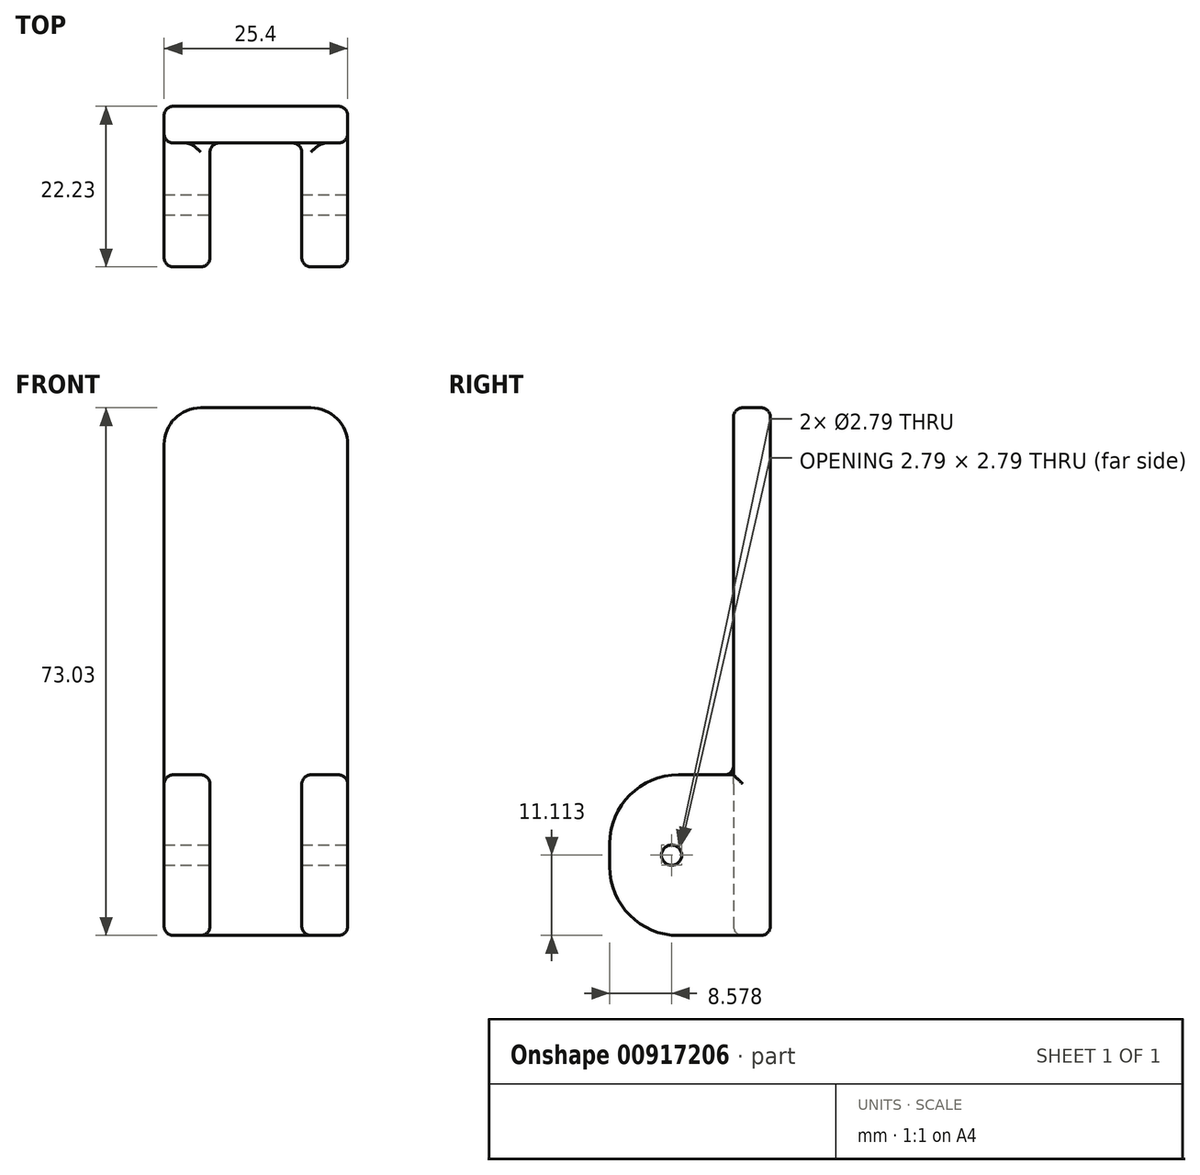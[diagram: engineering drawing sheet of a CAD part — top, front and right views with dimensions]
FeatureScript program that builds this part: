
annotation { "Feature Type Name" : "Feature", "Feature Type Description" : "" }
export const myFeature = defineFeature(function(context is Context, id is Id, definition is map)
    precondition{}
    {
        {
            var Q0;
            Q0=qCreatedBy(makeId("Top.planeOp"),FACE);
            var sketch = newSketch(context, id + "F0", { "sketchPlane" : qUnion([Q0])});
            skLineSegment(sketch, "E0", {"start": v(-12.7, 0) * mm, "end": v(12.7, 0) * mm});
            skLineSegment(sketch, "E1", {"start": v(12.7, 0) * mm, "end": v(12.7, -22.23) * mm});
            skLineSegment(sketch, "E2", {"start": v(12.7, -22.22) * mm, "end": v(6.35, -22.22) * mm});
            skLineSegment(sketch, "E3", {"start": v(6.35, -22.23) * mm, "end": v(6.35, -5.08) * mm});
            skLineSegment(sketch, "E4", {"start": v(6.35, -5.08) * mm, "end": v(-6.35, -5.08) * mm});
            skLineSegment(sketch, "E5", {"start": v(-6.35, -5.08) * mm, "end": v(-6.35, -22.23) * mm});
            skLineSegment(sketch, "E6", {"start": v(-6.35, -22.23) * mm, "end": v(-12.7, -22.23) * mm});
            skLineSegment(sketch, "E7", {"start": v(-12.7, -22.23) * mm, "end": v(-12.7, 0) * mm});
            skSolve(sketch);
        }
        {
            var Q0;
            Q0=makeQuery(id+"F0.imprint","IMPRINT",FACE,{"disambiguationData":[TD([[makeQuery(id+"F0.imprint","IMPRINT",EDGE,{"derivedFrom":sQuery(id+"F0.wireOp",EDGE,"E0")}),-1.0]])]});
            extrude(context, id + "F1", {"entities" : qUnion([Q0]), "depth" : 22.22 * mm, "offsetDistance" : 25.4 * mm});
        }
        {
            var Q0;
            Q0=makeQuery(id+"F1.opExtrude","CAP_FACE",FACE,{"disambiguationData":[OSD([sQuery(id+"F0.wireOp",EDGE,"E0"),sQuery(id+"F0.wireOp",EDGE,"E1"),sQuery(id+"F0.wireOp",EDGE,"E2"),sQuery(id+"F0.wireOp",EDGE,"E3"),sQuery(id+"F0.wireOp",EDGE,"E4"),sQuery(id+"F0.wireOp",EDGE,"E5"),sQuery(id+"F0.wireOp",EDGE,"E6"),sQuery(id+"F0.wireOp",EDGE,"E7")])],"isStart":false});
            var sketch = newSketch(context, id + "F2", { "sketchPlane" : qUnion([Q0])});
            skLineSegment(sketch, "E8.bottom", {"start": v(-12.7, 0) * mm, "end": v(12.7, 0) * mm});
            skLineSegment(sketch, "E8.top", {"start": v(-12.7, -5.08) * mm, "end": v(12.7, -5.08) * mm});
            skLineSegment(sketch, "E8.left", {"start": v(-12.7, 0) * mm, "end": v(-12.7, -5.08) * mm});
            skLineSegment(sketch, "E8.right", {"start": v(12.7, 0) * mm, "end": v(12.7, -5.08) * mm});
            skSolve(sketch);
        }
        {
            var Q0;
            Q0=makeQuery(id+"F2.imprint","IMPRINT",FACE,{"disambiguationData":[TD([[makeQuery(id+"F2.imprint","IMPRINT",EDGE,{"derivedFrom":sQuery(id+"F2.wireOp",EDGE,"E8.bottom")}),-1.0]])]});
            extrude(context, id + "F3", {"entities" : qUnion([Q0]), "operationType" : NewBodyOperationType.ADD, "depth" : 50.8 * mm, "offsetDistance" : 25.4 * mm});
        }
        {
            var Q0;
            Q0=makeQuery(id+"F3.boolean.opBoolean","MERGE",FACE,{"derivedFrom":[makeQuery(id+"F1.opExtrude","SWEPT_FACE",FACE,{"disambiguationData":[OSD([sQuery(id+"F0.wireOp",EDGE,"E1")])]}),makeQuery(id+"F3.opExtrude","SWEPT_FACE",FACE,{"disambiguationData":[OSD([sQuery(id+"F2.wireOp",EDGE,"E8.right")])]})]});
            var sketch = newSketch(context, id + "F4", { "sketchPlane" : qUnion([Q0])});
            skCircle(sketch, "E9", {"center": v(-13.65, 11.11) * mm, "radius": 1.4 * mm});
            skLineSegment(sketch, "E10", {"start": v(-22.23, 11.11) * mm, "end": v(-40.67, 11.11) * mm, "construction": true});
            skLineSegment(sketch, "E11", {"start": v(-13.65, 22.23) * mm, "end": v(-13.65, -2.66) * mm, "construction": true});
            skSolve(sketch);
        }
        {
            var Q0;
            Q0=makeQuery(id+"F4.imprint","IMPRINT",FACE,{"disambiguationData":[TD([[makeQuery(id+"F4.imprint","IMPRINT",EDGE,{"derivedFrom":sQuery(id+"F4.wireOp",EDGE,"E9")}),1.0]])]});
            extrude(context, id + "F5", {"entities" : qUnion([Q0]), "operationType" : NewBodyOperationType.REMOVE, "endBound" : BoundingType.THROUGH_ALL, "oppositeDirection" : true, "depth" : 25.4 * mm, "offsetDistance" : 25.4 * mm});
        }
        {
            var Q0;
            Q0=makeQuery(id+"F1.opExtrude","CAP_EDGE",EDGE,{"disambiguationData":[OSD([sQuery(id+"F0.wireOp",EDGE,"E2")])],"isStart":false});
            var Q1;
            Q1=makeQuery(id+"F1.opExtrude","CAP_EDGE",EDGE,{"disambiguationData":[OSD([sQuery(id+"F0.wireOp",EDGE,"E6")])],"isStart":false});
            var Q2;
            Q2=makeQuery(id+"F1.opExtrude","CAP_EDGE",EDGE,{"disambiguationData":[OSD([sQuery(id+"F0.wireOp",EDGE,"E6")])],"isStart":true});
            var Q3;
            Q3=makeQuery(id+"F1.opExtrude","CAP_EDGE",EDGE,{"disambiguationData":[OSD([sQuery(id+"F0.wireOp",EDGE,"E2")])],"isStart":true});
            fillet(context, id + "F6", {"entities" : qUnion([Q0, Q1, Q2, Q3]), "radius" : 9.52 * mm, "tangentPropagation" : true, "allowEdgeOverflow" : false});
        }
        {
            var Q0;
            Q0=makeQuery(id+"F3.opExtrude","CAP_EDGE",EDGE,{"disambiguationData":[OSD([sQuery(id+"F2.wireOp",EDGE,"E8.right")])],"isStart":false});
            var Q1;
            Q1=makeQuery(id+"F3.opExtrude","CAP_EDGE",EDGE,{"disambiguationData":[OSD([sQuery(id+"F2.wireOp",EDGE,"E8.left")])],"isStart":false});
            var Q2;
            {var subQ2=sQuery(id+"F0.wireOp",EDGE,"E1");var subQ3=sQuery(id+"F2.wireOp",EDGE,"E8.top");Q2=makeQuery(id+"F3.boolean.opBoolean","SPLIT",EDGE,{"disambiguationData":[TD([makeQuery(id+"F1.opExtrude","SWEPT_FACE",FACE,{"disambiguationData":[OSD([subQ2])]})])],"derivedFrom":makeQuery(id+"F3.opExtrude","CAP_EDGE",EDGE,{"disambiguationData":[OSD([subQ3])],"isStart":true})});}
            var Q3;
            {var subQ2=sQuery(id+"F0.wireOp",EDGE,"E5");var subQ3=sQuery(id+"F2.wireOp",EDGE,"E8.top");Q3=makeQuery(id+"F3.boolean.opBoolean","SPLIT",EDGE,{"disambiguationData":[TD([makeQuery(id+"F1.opExtrude","SWEPT_FACE",FACE,{"disambiguationData":[OSD([subQ2])]})])],"derivedFrom":makeQuery(id+"F3.opExtrude","CAP_EDGE",EDGE,{"disambiguationData":[OSD([subQ3])],"isStart":true})});}
            fillet(context, id + "F7", {"entities" : qUnion([Q0, Q1, Q2, Q3]), "radius" : 5.08 * mm, "tangentPropagation" : true, "allowEdgeOverflow" : false});
        }
        {
            var Q0;
            Q0=makeQuery(id+"F6.opFillet","BLEND_EDGE",EDGE,{"blendedFrom":[makeQuery(id+"F1.opExtrude","CAP_EDGE",EDGE,{"disambiguationData":[OSD([sQuery(id+"F0.wireOp",EDGE,"E6")])],"isStart":true}),makeQuery(id+"F3.boolean.opBoolean","MERGE",FACE,{"derivedFrom":[makeQuery(id+"F1.opExtrude","SWEPT_FACE",FACE,{"disambiguationData":[OSD([sQuery(id+"F0.wireOp",EDGE,"E7")])]}),makeQuery(id+"F3.opExtrude","SWEPT_FACE",FACE,{"disambiguationData":[OSD([sQuery(id+"F2.wireOp",EDGE,"E8.left")])]})]})],"blendedInto":[makeQuery(id+"F3.boolean.opBoolean","MERGE",FACE,{"derivedFrom":[makeQuery(id+"F1.opExtrude","SWEPT_FACE",FACE,{"disambiguationData":[OSD([sQuery(id+"F0.wireOp",EDGE,"E7")])]}),makeQuery(id+"F3.opExtrude","SWEPT_FACE",FACE,{"disambiguationData":[OSD([sQuery(id+"F2.wireOp",EDGE,"E8.left")])]})]})]});
            var Q1;
            Q1=makeQuery(id+"F6.opFillet","BLEND_EDGE",EDGE,{"blendedFrom":[makeQuery(id+"F1.opExtrude","CAP_EDGE",EDGE,{"disambiguationData":[OSD([sQuery(id+"F0.wireOp",EDGE,"E6")])],"isStart":false}),makeQuery(id+"F3.boolean.opBoolean","MERGE",FACE,{"derivedFrom":[makeQuery(id+"F1.opExtrude","SWEPT_FACE",FACE,{"disambiguationData":[OSD([sQuery(id+"F0.wireOp",EDGE,"E7")])]}),makeQuery(id+"F3.opExtrude","SWEPT_FACE",FACE,{"disambiguationData":[OSD([sQuery(id+"F2.wireOp",EDGE,"E8.left")])]})]})],"blendedInto":[makeQuery(id+"F3.boolean.opBoolean","MERGE",FACE,{"derivedFrom":[makeQuery(id+"F1.opExtrude","SWEPT_FACE",FACE,{"disambiguationData":[OSD([sQuery(id+"F0.wireOp",EDGE,"E7")])]}),makeQuery(id+"F3.opExtrude","SWEPT_FACE",FACE,{"disambiguationData":[OSD([sQuery(id+"F2.wireOp",EDGE,"E8.left")])]})]})]});
            var Q2;
            Q2=makeQuery(id+"F6.opFillet","BLEND_EDGE",EDGE,{"blendedFrom":[makeQuery(id+"F1.opExtrude","CAP_EDGE",EDGE,{"disambiguationData":[OSD([sQuery(id+"F0.wireOp",EDGE,"E6")])],"isStart":true}),makeQuery(id+"F1.opExtrude","SWEPT_FACE",FACE,{"disambiguationData":[OSD([sQuery(id+"F0.wireOp",EDGE,"E5")])]})],"blendedInto":[makeQuery(id+"F1.opExtrude","SWEPT_FACE",FACE,{"disambiguationData":[OSD([sQuery(id+"F0.wireOp",EDGE,"E5")])]})]});
            var Q3;
            Q3=makeQuery(id+"F7.opFillet","BLEND_EDGE",EDGE,{"blendedFrom":[makeQuery(id+"F3.opExtrude","CAP_EDGE",EDGE,{"disambiguationData":[OSD([sQuery(id+"F2.wireOp",EDGE,"E8.right")])],"isStart":false}),makeQuery(id+"F3.boolean.opBoolean","MERGE",FACE,{"derivedFrom":[makeQuery(id+"F1.opExtrude","SWEPT_FACE",FACE,{"disambiguationData":[OSD([sQuery(id+"F0.wireOp",EDGE,"E4")])]}),makeQuery(id+"F3.opExtrude","SWEPT_FACE",FACE,{"disambiguationData":[OSD([sQuery(id+"F2.wireOp",EDGE,"E8.top")])]})]})],"blendedInto":[makeQuery(id+"F3.boolean.opBoolean","MERGE",FACE,{"derivedFrom":[makeQuery(id+"F1.opExtrude","SWEPT_FACE",FACE,{"disambiguationData":[OSD([sQuery(id+"F0.wireOp",EDGE,"E4")])]}),makeQuery(id+"F3.opExtrude","SWEPT_FACE",FACE,{"disambiguationData":[OSD([sQuery(id+"F2.wireOp",EDGE,"E8.top")])]})]})]});
            var Q4;
            Q4=makeQuery(id+"F3.boolean.opBoolean","MERGE",EDGE,{"derivedFrom":[makeQuery(id+"F1.opExtrude","SWEPT_EDGE",EDGE,{"disambiguationData":[OSD([sQuery(id+"F0.wireOp",EDGE,"E0"),sQuery(id+"F0.wireOp",EDGE,"E1")])]}),makeQuery(id+"F3.opExtrude","SWEPT_EDGE",EDGE,{"disambiguationData":[OSD([sQuery(id+"F2.wireOp",EDGE,"E8.bottom"),sQuery(id+"F2.wireOp",EDGE,"E8.right")])]})]});
            var Q5;
            Q5=makeQuery(id+"F3.opExtrude","SWEPT_EDGE",EDGE,{"disambiguationData":[OSD([sQuery(id+"F0.wireOp",EDGE,"E7"),sQuery(id+"F2.wireOp",EDGE,"E8.top"),sQuery(id+"F2.wireOp",EDGE,"E8.left")])]});
            var Q6;
            Q6=makeQuery(id+"F6.opFillet","BLEND_EDGE",EDGE,{"blendedFrom":[makeQuery(id+"F1.opExtrude","CAP_EDGE",EDGE,{"disambiguationData":[OSD([sQuery(id+"F0.wireOp",EDGE,"E6")])],"isStart":false}),makeQuery(id+"F1.opExtrude","SWEPT_FACE",FACE,{"disambiguationData":[OSD([sQuery(id+"F0.wireOp",EDGE,"E5")])]})],"blendedInto":[makeQuery(id+"F1.opExtrude","SWEPT_FACE",FACE,{"disambiguationData":[OSD([sQuery(id+"F0.wireOp",EDGE,"E5")])]})]});
            var Q7;
            Q7=makeQuery(id+"F3.opExtrude","SWEPT_EDGE",EDGE,{"disambiguationData":[OSD([sQuery(id+"F0.wireOp",EDGE,"E1"),sQuery(id+"F2.wireOp",EDGE,"E8.top"),sQuery(id+"F2.wireOp",EDGE,"E8.right")])]});
            var Q8;
            Q8=makeQuery(id+"F6.opFillet","BLEND_EDGE",EDGE,{"blendedFrom":[makeQuery(id+"F1.opExtrude","CAP_EDGE",EDGE,{"disambiguationData":[OSD([sQuery(id+"F0.wireOp",EDGE,"E2")])],"isStart":false}),makeQuery(id+"F1.opExtrude","SWEPT_FACE",FACE,{"disambiguationData":[OSD([sQuery(id+"F0.wireOp",EDGE,"E3")])]})],"blendedInto":[makeQuery(id+"F1.opExtrude","SWEPT_FACE",FACE,{"disambiguationData":[OSD([sQuery(id+"F0.wireOp",EDGE,"E3")])]})]});
            var Q9;
            Q9=makeQuery(id+"F6.opFillet","BLEND_EDGE",EDGE,{"blendedFrom":[makeQuery(id+"F1.opExtrude","CAP_EDGE",EDGE,{"disambiguationData":[OSD([sQuery(id+"F0.wireOp",EDGE,"E2")])],"isStart":false}),makeQuery(id+"F3.boolean.opBoolean","MERGE",FACE,{"derivedFrom":[makeQuery(id+"F1.opExtrude","SWEPT_FACE",FACE,{"disambiguationData":[OSD([sQuery(id+"F0.wireOp",EDGE,"E1")])]}),makeQuery(id+"F3.opExtrude","SWEPT_FACE",FACE,{"disambiguationData":[OSD([sQuery(id+"F2.wireOp",EDGE,"E8.right")])]})]})],"blendedInto":[makeQuery(id+"F3.boolean.opBoolean","MERGE",FACE,{"derivedFrom":[makeQuery(id+"F1.opExtrude","SWEPT_FACE",FACE,{"disambiguationData":[OSD([sQuery(id+"F0.wireOp",EDGE,"E1")])]}),makeQuery(id+"F3.opExtrude","SWEPT_FACE",FACE,{"disambiguationData":[OSD([sQuery(id+"F2.wireOp",EDGE,"E8.right")])]})]})]});
            var Q10;
            {var subQ0=sQuery(id+"F2.wireOp",EDGE,"E8.top");var subQ1=makeQuery(id+"F3.opExtrude","SWEPT_FACE",FACE,{"disambiguationData":[OSD([subQ0])]});var subQ2=sQuery(id+"F0.wireOp",EDGE,"E4");var subQ3=makeQuery(id+"F1.opExtrude","SWEPT_FACE",FACE,{"disambiguationData":[OSD([subQ2])]});var subQ5=sQuery(id+"F0.wireOp",EDGE,"E5");Q10=makeQuery(id+"F7.opFillet","BLEND_EDGE",EDGE,{"blendedFrom":[makeQuery(id+"F3.boolean.opBoolean","SPLIT",EDGE,{"disambiguationData":[TD([makeQuery(id+"F1.opExtrude","SWEPT_FACE",FACE,{"disambiguationData":[OSD([subQ5])]})])],"derivedFrom":makeQuery(id+"F3.opExtrude","CAP_EDGE",EDGE,{"disambiguationData":[OSD([subQ0])],"isStart":true})}),makeQuery(id+"F3.boolean.opBoolean","MERGE",FACE,{"derivedFrom":[subQ3,subQ1]})],"blendedInto":[makeQuery(id+"F3.boolean.opBoolean","MERGE",FACE,{"derivedFrom":[subQ3,subQ1]})]});}
            var Q11;
            Q11=makeQuery(id+"F6.opFillet","BLEND_EDGE",EDGE,{"blendedFrom":[makeQuery(id+"F1.opExtrude","CAP_EDGE",EDGE,{"disambiguationData":[OSD([sQuery(id+"F0.wireOp",EDGE,"E2")])],"isStart":true}),makeQuery(id+"F3.boolean.opBoolean","MERGE",FACE,{"derivedFrom":[makeQuery(id+"F1.opExtrude","SWEPT_FACE",FACE,{"disambiguationData":[OSD([sQuery(id+"F0.wireOp",EDGE,"E1")])]}),makeQuery(id+"F3.opExtrude","SWEPT_FACE",FACE,{"disambiguationData":[OSD([sQuery(id+"F2.wireOp",EDGE,"E8.right")])]})]})],"blendedInto":[makeQuery(id+"F3.boolean.opBoolean","MERGE",FACE,{"derivedFrom":[makeQuery(id+"F1.opExtrude","SWEPT_FACE",FACE,{"disambiguationData":[OSD([sQuery(id+"F0.wireOp",EDGE,"E1")])]}),makeQuery(id+"F3.opExtrude","SWEPT_FACE",FACE,{"disambiguationData":[OSD([sQuery(id+"F2.wireOp",EDGE,"E8.right")])]})]})]});
            var Q12;
            {var subQ0=sQuery(id+"F0.wireOp",EDGE,"E4");var subQ2=sQuery(id+"F0.wireOp",EDGE,"E3");var subQ4=sQuery(id+"F0.wireOp",EDGE,"E2");var subQ5=sQuery(id+"F0.wireOp",EDGE,"E1");var subQ6=makeQuery(id+"F1.opExtrude","SWEPT_FACE",FACE,{"disambiguationData":[OSD([subQ5])]});var subQ7=sQuery(id+"F2.wireOp",EDGE,"E8.top");var subQ10=makeQuery(id+"F1.opExtrude","CAP_FACE",FACE,{"disambiguationData":[OSD([sQuery(id+"F0.wireOp",EDGE,"E0"),subQ5,subQ4,subQ2,subQ0,sQuery(id+"F0.wireOp",EDGE,"E5"),sQuery(id+"F0.wireOp",EDGE,"E6"),sQuery(id+"F0.wireOp",EDGE,"E7")])],"isStart":false});Q12=makeQuery(id+"F7.opFillet","BLEND_EDGE",EDGE,{"blendedFrom":[makeQuery(id+"F3.boolean.opBoolean","SPLIT",EDGE,{"disambiguationData":[TD([subQ6])],"derivedFrom":makeQuery(id+"F3.opExtrude","CAP_EDGE",EDGE,{"disambiguationData":[OSD([subQ7])],"isStart":true})}),makeQuery(id+"F3.boolean.opBoolean","SPLIT",FACE,{"disambiguationData":[TD([subQ6])],"derivedFrom":subQ10})],"blendedInto":[makeQuery(id+"F3.boolean.opBoolean","SPLIT",FACE,{"disambiguationData":[TD([subQ6])],"derivedFrom":subQ10})]});}
            var Q13;
            Q13=makeQuery(id+"F3.opExtrude","CAP_EDGE",EDGE,{"disambiguationData":[OSD([sQuery(id+"F2.wireOp",EDGE,"E8.top")])],"isStart":false});
            var Q14;
            {var subQ0=sQuery(id+"F0.wireOp",EDGE,"E5");var subQ1=makeQuery(id+"F1.opExtrude","SWEPT_FACE",FACE,{"disambiguationData":[OSD([subQ0])]});var subQ4=sQuery(id+"F2.wireOp",EDGE,"E8.top");Q14=makeQuery(id+"F7.opFillet","BLEND_EDGE",EDGE,{"blendedFrom":[makeQuery(id+"F3.boolean.opBoolean","SPLIT",EDGE,{"disambiguationData":[TD([subQ1])],"derivedFrom":makeQuery(id+"F3.opExtrude","CAP_EDGE",EDGE,{"disambiguationData":[OSD([subQ4])],"isStart":true})}),subQ1],"blendedInto":[subQ1]});}
            var Q15;
            Q15=makeQuery(id+"F1.opExtrude","CAP_EDGE",EDGE,{"disambiguationData":[OSD([sQuery(id+"F0.wireOp",EDGE,"E7")])],"isStart":true});
            var Q16;
            Q16=makeQuery(id+"F1.opExtrude","CAP_EDGE",EDGE,{"disambiguationData":[OSD([sQuery(id+"F0.wireOp",EDGE,"E5")])],"isStart":true});
            var Q17;
            Q17=makeQuery(id+"F1.opExtrude","CAP_EDGE",EDGE,{"disambiguationData":[OSD([sQuery(id+"F0.wireOp",EDGE,"E1")])],"isStart":true});
            var Q18;
            Q18=makeQuery(id+"F1.opExtrude","SWEPT_EDGE",EDGE,{"disambiguationData":[OSD([sQuery(id+"F0.wireOp",EDGE,"E3"),sQuery(id+"F0.wireOp",EDGE,"E4")])]});
            var Q19;
            {var subQ0=sQuery(id+"F0.wireOp",EDGE,"E6");Q19=makeQuery(id+"F6.opFillet","BLEND_EDGE",EDGE,{"blendedFrom":[makeQuery(id+"F1.opExtrude","CAP_EDGE",EDGE,{"disambiguationData":[OSD([subQ0])],"isStart":true}),makeQuery(id+"F1.opExtrude","SWEPT_FACE",FACE,{"disambiguationData":[OSD([subQ0])]})],"blendedInto":[makeQuery(id+"F1.opExtrude","SWEPT_FACE",FACE,{"disambiguationData":[OSD([subQ0])]})]});}
            var Q20;
            Q20=makeQuery(id+"F1.opExtrude","SWEPT_EDGE",EDGE,{"disambiguationData":[OSD([sQuery(id+"F0.wireOp",EDGE,"E4"),sQuery(id+"F0.wireOp",EDGE,"E5")])]});
            var Q21;
            Q21=makeQuery(id+"F1.opExtrude","CAP_EDGE",EDGE,{"disambiguationData":[OSD([sQuery(id+"F0.wireOp",EDGE,"E3")])],"isStart":false});
            var Q22;
            Q22=makeQuery(id+"F7.opFillet","BLEND_EDGE",EDGE,{"blendedFrom":[makeQuery(id+"F3.opExtrude","CAP_EDGE",EDGE,{"disambiguationData":[OSD([sQuery(id+"F2.wireOp",EDGE,"E8.left")])],"isStart":false}),makeQuery(id+"F3.boolean.opBoolean","MERGE",FACE,{"derivedFrom":[makeQuery(id+"F1.opExtrude","SWEPT_FACE",FACE,{"disambiguationData":[OSD([sQuery(id+"F0.wireOp",EDGE,"E4")])]}),makeQuery(id+"F3.opExtrude","SWEPT_FACE",FACE,{"disambiguationData":[OSD([sQuery(id+"F2.wireOp",EDGE,"E8.top")])]})]})],"blendedInto":[makeQuery(id+"F3.boolean.opBoolean","MERGE",FACE,{"derivedFrom":[makeQuery(id+"F1.opExtrude","SWEPT_FACE",FACE,{"disambiguationData":[OSD([sQuery(id+"F0.wireOp",EDGE,"E4")])]}),makeQuery(id+"F3.opExtrude","SWEPT_FACE",FACE,{"disambiguationData":[OSD([sQuery(id+"F2.wireOp",EDGE,"E8.top")])]})]})]});
            var Q23;
            {var subQ0=sQuery(id+"F0.wireOp",EDGE,"E6");Q23=makeQuery(id+"F6.opFillet","BLEND_EDGE",EDGE,{"blendedFrom":[makeQuery(id+"F1.opExtrude","CAP_EDGE",EDGE,{"disambiguationData":[OSD([subQ0])],"isStart":true}),makeQuery(id+"F1.opExtrude","CAP_FACE",FACE,{"disambiguationData":[OSD([sQuery(id+"F0.wireOp",EDGE,"E0"),sQuery(id+"F0.wireOp",EDGE,"E1"),sQuery(id+"F0.wireOp",EDGE,"E2"),sQuery(id+"F0.wireOp",EDGE,"E3"),sQuery(id+"F0.wireOp",EDGE,"E4"),sQuery(id+"F0.wireOp",EDGE,"E5"),subQ0,sQuery(id+"F0.wireOp",EDGE,"E7")])],"isStart":true})],"blendedInto":[makeQuery(id+"F1.opExtrude","CAP_FACE",FACE,{"disambiguationData":[OSD([sQuery(id+"F0.wireOp",EDGE,"E0"),sQuery(id+"F0.wireOp",EDGE,"E1"),sQuery(id+"F0.wireOp",EDGE,"E2"),sQuery(id+"F0.wireOp",EDGE,"E3"),sQuery(id+"F0.wireOp",EDGE,"E4"),sQuery(id+"F0.wireOp",EDGE,"E5"),subQ0,sQuery(id+"F0.wireOp",EDGE,"E7")])],"isStart":true})]});}
            var Q24;
            Q24=makeQuery(id+"F1.opExtrude","CAP_EDGE",EDGE,{"disambiguationData":[OSD([sQuery(id+"F0.wireOp",EDGE,"E5")])],"isStart":false});
            var Q25;
            {var subQ0=sQuery(id+"F0.wireOp",EDGE,"E2");Q25=makeQuery(id+"F6.opFillet","BLEND_EDGE",EDGE,{"blendedFrom":[makeQuery(id+"F1.opExtrude","CAP_EDGE",EDGE,{"disambiguationData":[OSD([subQ0])],"isStart":true}),makeQuery(id+"F1.opExtrude","CAP_FACE",FACE,{"disambiguationData":[OSD([sQuery(id+"F0.wireOp",EDGE,"E0"),sQuery(id+"F0.wireOp",EDGE,"E1"),subQ0,sQuery(id+"F0.wireOp",EDGE,"E3"),sQuery(id+"F0.wireOp",EDGE,"E4"),sQuery(id+"F0.wireOp",EDGE,"E5"),sQuery(id+"F0.wireOp",EDGE,"E6"),sQuery(id+"F0.wireOp",EDGE,"E7")])],"isStart":true})],"blendedInto":[makeQuery(id+"F1.opExtrude","CAP_FACE",FACE,{"disambiguationData":[OSD([sQuery(id+"F0.wireOp",EDGE,"E0"),sQuery(id+"F0.wireOp",EDGE,"E1"),subQ0,sQuery(id+"F0.wireOp",EDGE,"E3"),sQuery(id+"F0.wireOp",EDGE,"E4"),sQuery(id+"F0.wireOp",EDGE,"E5"),sQuery(id+"F0.wireOp",EDGE,"E6"),sQuery(id+"F0.wireOp",EDGE,"E7")])],"isStart":true})]});}
            var Q26;
            Q26=makeQuery(id+"F1.opExtrude","CAP_EDGE",EDGE,{"disambiguationData":[OSD([sQuery(id+"F0.wireOp",EDGE,"E1")])],"isStart":false});
            var Q27;
            {var subQ0=sQuery(id+"F0.wireOp",EDGE,"E3");var subQ1=makeQuery(id+"F1.opExtrude","SWEPT_FACE",FACE,{"disambiguationData":[OSD([subQ0])]});var subQ3=sQuery(id+"F0.wireOp",EDGE,"E1");var subQ4=sQuery(id+"F2.wireOp",EDGE,"E8.top");Q27=makeQuery(id+"F7.opFillet","BLEND_EDGE",EDGE,{"blendedFrom":[makeQuery(id+"F3.boolean.opBoolean","SPLIT",EDGE,{"disambiguationData":[TD([makeQuery(id+"F1.opExtrude","SWEPT_FACE",FACE,{"disambiguationData":[OSD([subQ3])]})])],"derivedFrom":makeQuery(id+"F3.opExtrude","CAP_EDGE",EDGE,{"disambiguationData":[OSD([subQ4])],"isStart":true})}),subQ1],"blendedInto":[subQ1]});}
            var Q28;
            Q28=makeQuery(id+"F1.opExtrude","SWEPT_EDGE",EDGE,{"disambiguationData":[OSD([sQuery(id+"F0.wireOp",EDGE,"E6"),sQuery(id+"F0.wireOp",EDGE,"E7")])]});
            var Q29;
            Q29=makeQuery(id+"F3.boolean.opBoolean","MERGE",EDGE,{"derivedFrom":[makeQuery(id+"F1.opExtrude","SWEPT_EDGE",EDGE,{"disambiguationData":[OSD([sQuery(id+"F0.wireOp",EDGE,"E0"),sQuery(id+"F0.wireOp",EDGE,"E7")])]}),makeQuery(id+"F3.opExtrude","SWEPT_EDGE",EDGE,{"disambiguationData":[OSD([sQuery(id+"F2.wireOp",EDGE,"E8.bottom"),sQuery(id+"F2.wireOp",EDGE,"E8.left")])]})]});
            var Q30;
            {var subQ0=makeQuery(id+"F3.opExtrude","SWEPT_FACE",FACE,{"disambiguationData":[OSD([sQuery(id+"F2.wireOp",EDGE,"E8.right")])]});var subQ1=sQuery(id+"F0.wireOp",EDGE,"E1");var subQ2=makeQuery(id+"F1.opExtrude","SWEPT_FACE",FACE,{"disambiguationData":[OSD([subQ1])]});var subQ5=sQuery(id+"F2.wireOp",EDGE,"E8.top");Q30=makeQuery(id+"F7.opFillet","BLEND_EDGE",EDGE,{"blendedFrom":[makeQuery(id+"F3.boolean.opBoolean","SPLIT",EDGE,{"disambiguationData":[TD([subQ2])],"derivedFrom":makeQuery(id+"F3.opExtrude","CAP_EDGE",EDGE,{"disambiguationData":[OSD([subQ5])],"isStart":true})}),makeQuery(id+"F3.boolean.opBoolean","MERGE",FACE,{"derivedFrom":[subQ2,subQ0]})],"blendedInto":[makeQuery(id+"F3.boolean.opBoolean","MERGE",FACE,{"derivedFrom":[subQ2,subQ0]})]});}
            var Q31;
            Q31=makeQuery(id+"F7.opFillet","BLEND_EDGE",EDGE,{"blendedFrom":[makeQuery(id+"F3.opExtrude","CAP_EDGE",EDGE,{"disambiguationData":[OSD([sQuery(id+"F2.wireOp",EDGE,"E8.right")])],"isStart":false}),makeQuery(id+"F3.boolean.opBoolean","MERGE",FACE,{"derivedFrom":[makeQuery(id+"F1.opExtrude","SWEPT_FACE",FACE,{"disambiguationData":[OSD([sQuery(id+"F0.wireOp",EDGE,"E0")])]}),makeQuery(id+"F3.opExtrude","SWEPT_FACE",FACE,{"disambiguationData":[OSD([sQuery(id+"F2.wireOp",EDGE,"E8.bottom")])]})]})],"blendedInto":[makeQuery(id+"F3.boolean.opBoolean","MERGE",FACE,{"derivedFrom":[makeQuery(id+"F1.opExtrude","SWEPT_FACE",FACE,{"disambiguationData":[OSD([sQuery(id+"F0.wireOp",EDGE,"E0")])]}),makeQuery(id+"F3.opExtrude","SWEPT_FACE",FACE,{"disambiguationData":[OSD([sQuery(id+"F2.wireOp",EDGE,"E8.bottom")])]})]})]});
            var Q32;
            {var subQ0=sQuery(id+"F0.wireOp",EDGE,"E4");var subQ1=sQuery(id+"F0.wireOp",EDGE,"E3");var subQ2=sQuery(id+"F0.wireOp",EDGE,"E2");var subQ3=sQuery(id+"F0.wireOp",EDGE,"E1");Q32=makeQuery(id+"F6.opFillet","BLEND_EDGE",EDGE,{"blendedFrom":[makeQuery(id+"F1.opExtrude","CAP_EDGE",EDGE,{"disambiguationData":[OSD([subQ2])],"isStart":false}),makeQuery(id+"F3.boolean.opBoolean","SPLIT",FACE,{"disambiguationData":[TD([makeQuery(id+"F1.opExtrude","SWEPT_FACE",FACE,{"disambiguationData":[OSD([subQ3])]})])],"derivedFrom":makeQuery(id+"F1.opExtrude","CAP_FACE",FACE,{"disambiguationData":[OSD([sQuery(id+"F0.wireOp",EDGE,"E0"),subQ3,subQ2,subQ1,subQ0,sQuery(id+"F0.wireOp",EDGE,"E5"),sQuery(id+"F0.wireOp",EDGE,"E6"),sQuery(id+"F0.wireOp",EDGE,"E7")])],"isStart":false})})],"blendedInto":[makeQuery(id+"F3.boolean.opBoolean","SPLIT",FACE,{"disambiguationData":[TD([makeQuery(id+"F1.opExtrude","SWEPT_FACE",FACE,{"disambiguationData":[OSD([subQ3])]})])],"derivedFrom":makeQuery(id+"F1.opExtrude","CAP_FACE",FACE,{"disambiguationData":[OSD([sQuery(id+"F0.wireOp",EDGE,"E0"),subQ3,subQ2,subQ1,subQ0,sQuery(id+"F0.wireOp",EDGE,"E5"),sQuery(id+"F0.wireOp",EDGE,"E6"),sQuery(id+"F0.wireOp",EDGE,"E7")])],"isStart":false})})]});}
            var Q33;
            {var subQ0=sQuery(id+"F0.wireOp",EDGE,"E6");Q33=makeQuery(id+"F6.opFillet","BLEND_EDGE",EDGE,{"blendedFrom":[makeQuery(id+"F1.opExtrude","CAP_EDGE",EDGE,{"disambiguationData":[OSD([subQ0])],"isStart":false}),makeQuery(id+"F1.opExtrude","SWEPT_FACE",FACE,{"disambiguationData":[OSD([subQ0])]})],"blendedInto":[makeQuery(id+"F1.opExtrude","SWEPT_FACE",FACE,{"disambiguationData":[OSD([subQ0])]})]});}
            var Q34;
            Q34=makeQuery(id+"F6.opFillet","BLEND_EDGE",EDGE,{"blendedFrom":[makeQuery(id+"F1.opExtrude","CAP_EDGE",EDGE,{"disambiguationData":[OSD([sQuery(id+"F0.wireOp",EDGE,"E2")])],"isStart":true}),makeQuery(id+"F1.opExtrude","SWEPT_FACE",FACE,{"disambiguationData":[OSD([sQuery(id+"F0.wireOp",EDGE,"E3")])]})],"blendedInto":[makeQuery(id+"F1.opExtrude","SWEPT_FACE",FACE,{"disambiguationData":[OSD([sQuery(id+"F0.wireOp",EDGE,"E3")])]})]});
            var Q35;
            Q35=makeQuery(id+"F1.opExtrude","CAP_EDGE",EDGE,{"disambiguationData":[OSD([sQuery(id+"F0.wireOp",EDGE,"E0")])],"isStart":true});
            var Q36;
            {var subQ0=sQuery(id+"F0.wireOp",EDGE,"E7");var subQ1=sQuery(id+"F0.wireOp",EDGE,"E6");var subQ2=sQuery(id+"F0.wireOp",EDGE,"E5");var subQ3=sQuery(id+"F0.wireOp",EDGE,"E4");Q36=makeQuery(id+"F6.opFillet","BLEND_EDGE",EDGE,{"blendedFrom":[makeQuery(id+"F1.opExtrude","CAP_EDGE",EDGE,{"disambiguationData":[OSD([subQ1])],"isStart":false}),makeQuery(id+"F3.boolean.opBoolean","SPLIT",FACE,{"disambiguationData":[TD([makeQuery(id+"F1.opExtrude","SWEPT_FACE",FACE,{"disambiguationData":[OSD([subQ2])]})])],"derivedFrom":makeQuery(id+"F1.opExtrude","CAP_FACE",FACE,{"disambiguationData":[OSD([sQuery(id+"F0.wireOp",EDGE,"E0"),sQuery(id+"F0.wireOp",EDGE,"E1"),sQuery(id+"F0.wireOp",EDGE,"E2"),sQuery(id+"F0.wireOp",EDGE,"E3"),subQ3,subQ2,subQ1,subQ0])],"isStart":false})})],"blendedInto":[makeQuery(id+"F3.boolean.opBoolean","SPLIT",FACE,{"disambiguationData":[TD([makeQuery(id+"F1.opExtrude","SWEPT_FACE",FACE,{"disambiguationData":[OSD([subQ2])]})])],"derivedFrom":makeQuery(id+"F1.opExtrude","CAP_FACE",FACE,{"disambiguationData":[OSD([sQuery(id+"F0.wireOp",EDGE,"E0"),sQuery(id+"F0.wireOp",EDGE,"E1"),sQuery(id+"F0.wireOp",EDGE,"E2"),sQuery(id+"F0.wireOp",EDGE,"E3"),subQ3,subQ2,subQ1,subQ0])],"isStart":false})})]});}
            var Q37;
            {var subQ0=sQuery(id+"F2.wireOp",EDGE,"E8.right");Q37=makeQuery(id+"F7.opFillet","BLEND_EDGE",EDGE,{"blendedFrom":[makeQuery(id+"F3.opExtrude","CAP_EDGE",EDGE,{"disambiguationData":[OSD([subQ0])],"isStart":false}),makeQuery(id+"F3.boolean.opBoolean","MERGE",FACE,{"derivedFrom":[makeQuery(id+"F1.opExtrude","SWEPT_FACE",FACE,{"disambiguationData":[OSD([sQuery(id+"F0.wireOp",EDGE,"E1")])]}),makeQuery(id+"F3.opExtrude","SWEPT_FACE",FACE,{"disambiguationData":[OSD([subQ0])]})]})],"blendedInto":[makeQuery(id+"F3.boolean.opBoolean","MERGE",FACE,{"derivedFrom":[makeQuery(id+"F1.opExtrude","SWEPT_FACE",FACE,{"disambiguationData":[OSD([sQuery(id+"F0.wireOp",EDGE,"E1")])]}),makeQuery(id+"F3.opExtrude","SWEPT_FACE",FACE,{"disambiguationData":[OSD([subQ0])]})]})]});}
            var Q38;
            {var subQ0=sQuery(id+"F2.wireOp",EDGE,"E8.top");var subQ1=makeQuery(id+"F3.opExtrude","SWEPT_FACE",FACE,{"disambiguationData":[OSD([subQ0])]});var subQ2=sQuery(id+"F0.wireOp",EDGE,"E4");var subQ3=makeQuery(id+"F1.opExtrude","SWEPT_FACE",FACE,{"disambiguationData":[OSD([subQ2])]});var subQ5=sQuery(id+"F0.wireOp",EDGE,"E1");Q38=makeQuery(id+"F7.opFillet","BLEND_EDGE",EDGE,{"blendedFrom":[makeQuery(id+"F3.boolean.opBoolean","SPLIT",EDGE,{"disambiguationData":[TD([makeQuery(id+"F1.opExtrude","SWEPT_FACE",FACE,{"disambiguationData":[OSD([subQ5])]})])],"derivedFrom":makeQuery(id+"F3.opExtrude","CAP_EDGE",EDGE,{"disambiguationData":[OSD([subQ0])],"isStart":true})}),makeQuery(id+"F3.boolean.opBoolean","MERGE",FACE,{"derivedFrom":[subQ3,subQ1]})],"blendedInto":[makeQuery(id+"F3.boolean.opBoolean","MERGE",FACE,{"derivedFrom":[subQ3,subQ1]})]});}
            var Q39;
            Q39=makeQuery(id+"F1.opExtrude","SWEPT_EDGE",EDGE,{"disambiguationData":[OSD([sQuery(id+"F0.wireOp",EDGE,"E5"),sQuery(id+"F0.wireOp",EDGE,"E6")])]});
            var Q40;
            Q40=makeQuery(id+"F3.opExtrude","CAP_EDGE",EDGE,{"disambiguationData":[OSD([sQuery(id+"F2.wireOp",EDGE,"E8.bottom")])],"isStart":false});
            var Q41;
            {var subQ0=sQuery(id+"F0.wireOp",EDGE,"E2");Q41=makeQuery(id+"F6.opFillet","BLEND_EDGE",EDGE,{"blendedFrom":[makeQuery(id+"F1.opExtrude","CAP_EDGE",EDGE,{"disambiguationData":[OSD([subQ0])],"isStart":false}),makeQuery(id+"F1.opExtrude","SWEPT_FACE",FACE,{"disambiguationData":[OSD([subQ0])]})],"blendedInto":[makeQuery(id+"F1.opExtrude","SWEPT_FACE",FACE,{"disambiguationData":[OSD([subQ0])]})]});}
            var Q42;
            {var subQ0=sQuery(id+"F2.wireOp",EDGE,"E8.left");Q42=makeQuery(id+"F7.opFillet","BLEND_EDGE",EDGE,{"blendedFrom":[makeQuery(id+"F3.opExtrude","CAP_EDGE",EDGE,{"disambiguationData":[OSD([subQ0])],"isStart":false}),makeQuery(id+"F3.boolean.opBoolean","MERGE",FACE,{"derivedFrom":[makeQuery(id+"F1.opExtrude","SWEPT_FACE",FACE,{"disambiguationData":[OSD([sQuery(id+"F0.wireOp",EDGE,"E7")])]}),makeQuery(id+"F3.opExtrude","SWEPT_FACE",FACE,{"disambiguationData":[OSD([subQ0])]})]})],"blendedInto":[makeQuery(id+"F3.boolean.opBoolean","MERGE",FACE,{"derivedFrom":[makeQuery(id+"F1.opExtrude","SWEPT_FACE",FACE,{"disambiguationData":[OSD([sQuery(id+"F0.wireOp",EDGE,"E7")])]}),makeQuery(id+"F3.opExtrude","SWEPT_FACE",FACE,{"disambiguationData":[OSD([subQ0])]})]})]});}
            var Q43;
            Q43=makeQuery(id+"F1.opExtrude","CAP_EDGE",EDGE,{"disambiguationData":[OSD([sQuery(id+"F0.wireOp",EDGE,"E7")])],"isStart":false});
            var Q44;
            {var subQ0=makeQuery(id+"F3.opExtrude","SWEPT_FACE",FACE,{"disambiguationData":[OSD([sQuery(id+"F2.wireOp",EDGE,"E8.left")])]});var subQ1=sQuery(id+"F0.wireOp",EDGE,"E7");var subQ2=makeQuery(id+"F1.opExtrude","SWEPT_FACE",FACE,{"disambiguationData":[OSD([subQ1])]});var subQ4=sQuery(id+"F0.wireOp",EDGE,"E5");var subQ5=sQuery(id+"F2.wireOp",EDGE,"E8.top");Q44=makeQuery(id+"F7.opFillet","BLEND_EDGE",EDGE,{"blendedFrom":[makeQuery(id+"F3.boolean.opBoolean","SPLIT",EDGE,{"disambiguationData":[TD([makeQuery(id+"F1.opExtrude","SWEPT_FACE",FACE,{"disambiguationData":[OSD([subQ4])]})])],"derivedFrom":makeQuery(id+"F3.opExtrude","CAP_EDGE",EDGE,{"disambiguationData":[OSD([subQ5])],"isStart":true})}),makeQuery(id+"F3.boolean.opBoolean","MERGE",FACE,{"derivedFrom":[subQ2,subQ0]})],"blendedInto":[makeQuery(id+"F3.boolean.opBoolean","MERGE",FACE,{"derivedFrom":[subQ2,subQ0]})]});}
            var Q45;
            Q45=makeQuery(id+"F1.opExtrude","CAP_EDGE",EDGE,{"disambiguationData":[OSD([sQuery(id+"F0.wireOp",EDGE,"E3")])],"isStart":true});
            var Q46;
            {var subQ0=sQuery(id+"F2.wireOp",EDGE,"E8.right");Q46=makeQuery(id+"F7.opFillet","BLEND_EDGE",EDGE,{"blendedFrom":[makeQuery(id+"F3.opExtrude","CAP_EDGE",EDGE,{"disambiguationData":[OSD([subQ0])],"isStart":false}),makeQuery(id+"F3.opExtrude","CAP_FACE",FACE,{"disambiguationData":[OSD([sQuery(id+"F2.wireOp",EDGE,"E8.bottom"),sQuery(id+"F2.wireOp",EDGE,"E8.top"),sQuery(id+"F2.wireOp",EDGE,"E8.left"),subQ0])],"isStart":false})],"blendedInto":[makeQuery(id+"F3.opExtrude","CAP_FACE",FACE,{"disambiguationData":[OSD([sQuery(id+"F2.wireOp",EDGE,"E8.bottom"),sQuery(id+"F2.wireOp",EDGE,"E8.top"),sQuery(id+"F2.wireOp",EDGE,"E8.left"),subQ0])],"isStart":false})]});}
            var Q47;
            Q47=makeQuery(id+"F7.opFillet","BLEND_EDGE",EDGE,{"blendedFrom":[makeQuery(id+"F3.opExtrude","CAP_EDGE",EDGE,{"disambiguationData":[OSD([sQuery(id+"F2.wireOp",EDGE,"E8.left")])],"isStart":false}),makeQuery(id+"F3.boolean.opBoolean","MERGE",FACE,{"derivedFrom":[makeQuery(id+"F1.opExtrude","SWEPT_FACE",FACE,{"disambiguationData":[OSD([sQuery(id+"F0.wireOp",EDGE,"E0")])]}),makeQuery(id+"F3.opExtrude","SWEPT_FACE",FACE,{"disambiguationData":[OSD([sQuery(id+"F2.wireOp",EDGE,"E8.bottom")])]})]})],"blendedInto":[makeQuery(id+"F3.boolean.opBoolean","MERGE",FACE,{"derivedFrom":[makeQuery(id+"F1.opExtrude","SWEPT_FACE",FACE,{"disambiguationData":[OSD([sQuery(id+"F0.wireOp",EDGE,"E0")])]}),makeQuery(id+"F3.opExtrude","SWEPT_FACE",FACE,{"disambiguationData":[OSD([sQuery(id+"F2.wireOp",EDGE,"E8.bottom")])]})]})]});
            var Q48;
            {var subQ0=sQuery(id+"F0.wireOp",EDGE,"E7");var subQ3=sQuery(id+"F0.wireOp",EDGE,"E6");var subQ4=sQuery(id+"F2.wireOp",EDGE,"E8.top");var subQ6=sQuery(id+"F0.wireOp",EDGE,"E5");var subQ7=makeQuery(id+"F1.opExtrude","SWEPT_FACE",FACE,{"disambiguationData":[OSD([subQ6])]});var subQ8=sQuery(id+"F0.wireOp",EDGE,"E4");var subQ10=makeQuery(id+"F1.opExtrude","CAP_FACE",FACE,{"disambiguationData":[OSD([sQuery(id+"F0.wireOp",EDGE,"E0"),sQuery(id+"F0.wireOp",EDGE,"E1"),sQuery(id+"F0.wireOp",EDGE,"E2"),sQuery(id+"F0.wireOp",EDGE,"E3"),subQ8,subQ6,subQ3,subQ0])],"isStart":false});Q48=makeQuery(id+"F7.opFillet","BLEND_EDGE",EDGE,{"blendedFrom":[makeQuery(id+"F3.boolean.opBoolean","SPLIT",EDGE,{"disambiguationData":[TD([subQ7])],"derivedFrom":makeQuery(id+"F3.opExtrude","CAP_EDGE",EDGE,{"disambiguationData":[OSD([subQ4])],"isStart":true})}),makeQuery(id+"F3.boolean.opBoolean","SPLIT",FACE,{"disambiguationData":[TD([subQ7])],"derivedFrom":subQ10})],"blendedInto":[makeQuery(id+"F3.boolean.opBoolean","SPLIT",FACE,{"disambiguationData":[TD([subQ7])],"derivedFrom":subQ10})]});}
            var Q49;
            Q49=makeQuery(id+"F1.opExtrude","CAP_EDGE",EDGE,{"disambiguationData":[OSD([sQuery(id+"F0.wireOp",EDGE,"E4")])],"isStart":true});
            var Q50;
            Q50=makeQuery(id+"F1.opExtrude","SWEPT_EDGE",EDGE,{"disambiguationData":[OSD([sQuery(id+"F0.wireOp",EDGE,"E1"),sQuery(id+"F0.wireOp",EDGE,"E2")])]});
            var Q51;
            {var subQ0=sQuery(id+"F0.wireOp",EDGE,"E2");Q51=makeQuery(id+"F6.opFillet","BLEND_EDGE",EDGE,{"blendedFrom":[makeQuery(id+"F1.opExtrude","CAP_EDGE",EDGE,{"disambiguationData":[OSD([subQ0])],"isStart":true}),makeQuery(id+"F1.opExtrude","SWEPT_FACE",FACE,{"disambiguationData":[OSD([subQ0])]})],"blendedInto":[makeQuery(id+"F1.opExtrude","SWEPT_FACE",FACE,{"disambiguationData":[OSD([subQ0])]})]});}
            var Q52;
            {var subQ0=sQuery(id+"F2.wireOp",EDGE,"E8.left");Q52=makeQuery(id+"F7.opFillet","BLEND_EDGE",EDGE,{"blendedFrom":[makeQuery(id+"F3.opExtrude","CAP_EDGE",EDGE,{"disambiguationData":[OSD([subQ0])],"isStart":false}),makeQuery(id+"F3.opExtrude","CAP_FACE",FACE,{"disambiguationData":[OSD([sQuery(id+"F2.wireOp",EDGE,"E8.bottom"),sQuery(id+"F2.wireOp",EDGE,"E8.top"),subQ0,sQuery(id+"F2.wireOp",EDGE,"E8.right")])],"isStart":false})],"blendedInto":[makeQuery(id+"F3.opExtrude","CAP_FACE",FACE,{"disambiguationData":[OSD([sQuery(id+"F2.wireOp",EDGE,"E8.bottom"),sQuery(id+"F2.wireOp",EDGE,"E8.top"),subQ0,sQuery(id+"F2.wireOp",EDGE,"E8.right")])],"isStart":false})]});}
            var Q53;
            Q53=makeQuery(id+"F1.opExtrude","SWEPT_EDGE",EDGE,{"disambiguationData":[OSD([sQuery(id+"F0.wireOp",EDGE,"E2"),sQuery(id+"F0.wireOp",EDGE,"E3")])]});
            fillet(context, id + "F8", {"entities" : qUnion([Q0, Q1, Q2, Q3, Q4, Q5, Q6, Q7, Q8, Q9, Q10, Q11, Q12, Q13, Q14, Q15, Q16, Q17, Q18, Q19, Q20, Q21, Q22, Q23, Q24, Q25, Q26, Q27, Q28, Q29, Q30, Q31, Q32, Q33, Q34, Q35, Q36, Q37, Q38, Q39, Q40, Q41, Q42, Q43, Q44, Q45, Q46, Q47, Q48, Q49, Q50, Q51, Q52, Q53]), "radius" : 1.27 * mm, "tangentPropagation" : true, "allowEdgeOverflow" : false});
        }
    });
